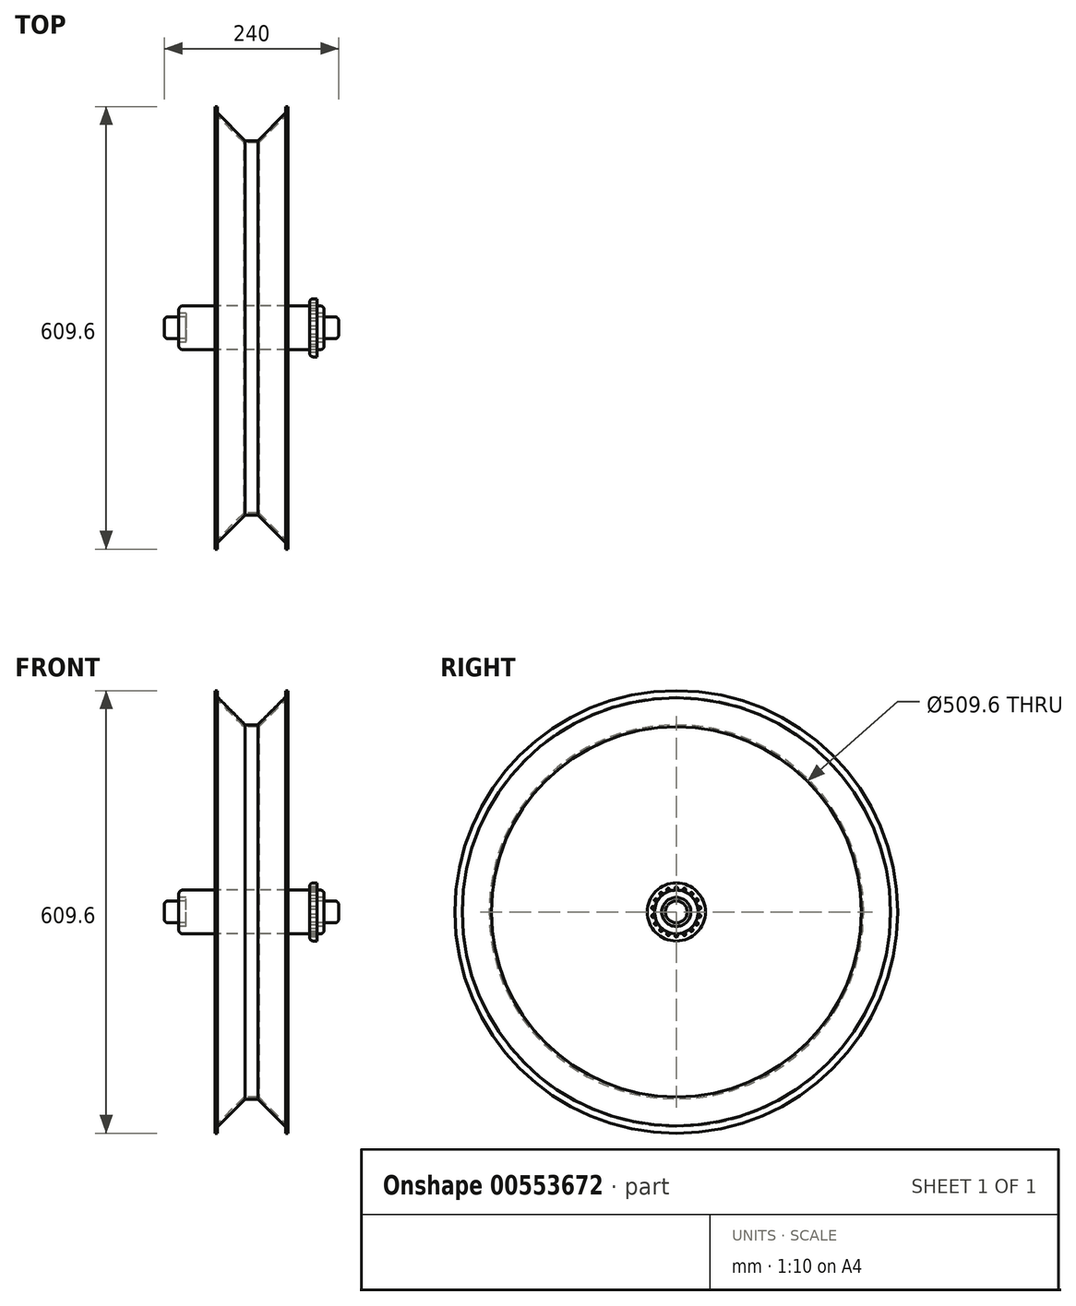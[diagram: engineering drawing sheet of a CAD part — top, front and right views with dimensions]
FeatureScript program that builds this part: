
annotation { "Feature Type Name" : "Feature", "Feature Type Description" : "" }
export const myFeature = defineFeature(function(context is Context, id is Id, definition is map)
    precondition{}
    {
        {
            var Q0;
            Q0=qCreatedBy(makeId("Front.planeOp"),FACE);
            var sketch = newSketch(context, id + "F0", { "sketchPlane" : qUnion([Q0])});
            skLineSegment(sketch, "E0", {"start": v(0, 0) * mm, "end": v(0, 304.8) * mm, "construction": true});
            skLineSegment(sketch, "E1", {"start": v(0, 0) * mm, "end": v(0, 254.8) * mm, "construction": true});
            skLineSegment(sketch, "E2", {"start": v(0, 304.8) * mm, "end": v(-50, 304.8) * mm, "construction": true});
            skLineSegment(sketch, "E3", {"start": v(0, 304.8) * mm, "end": v(50, 304.8) * mm, "construction": true});
            skPoint(sketch, "E4", {"position": v(-50, 304.8) * mm});
            skPoint(sketch, "E5", {"position": v(50, 304.8) * mm});
            skLineSegment(sketch, "E6", {"start": v(-50, 294.8) * mm, "end": v(-10, 254.8) * mm});
            skLineSegment(sketch, "E7", {"start": v(-50, 294.8) * mm, "end": v(-50, 304.8) * mm});
            skLineSegment(sketch, "E8", {"start": v(-10, 254.8) * mm, "end": v(0, 254.8) * mm});
            skLineSegment(sketch, "E9", {"start": v(50, 304.8) * mm, "end": v(50, 294.8) * mm});
            skLineSegment(sketch, "E10", {"start": v(50, 294.8) * mm, "end": v(10, 254.8) * mm});
            skLineSegment(sketch, "E11", {"start": v(10, 254.8) * mm, "end": v(0, 254.8) * mm});
            skLineSegment(sketch, "E12.0", {"start": v(-47, 296.04) * mm, "end": v(-47, 304.8) * mm});
            skLineSegment(sketch, "E12.1", {"start": v(-47, 296.04) * mm, "end": v(-8.76, 257.8) * mm});
            skLineSegment(sketch, "E12.2", {"start": v(47, 304.8) * mm, "end": v(47, 296.04) * mm});
            skLineSegment(sketch, "E12.3", {"start": v(47, 296.04) * mm, "end": v(8.76, 257.8) * mm});
            skLineSegment(sketch, "E12.4", {"start": v(8.76, 257.8) * mm, "end": v(0, 257.8) * mm});
            skLineSegment(sketch, "E12.5", {"start": v(-8.76, 257.8) * mm, "end": v(0, 257.8) * mm});
            skLineSegment(sketch, "E13", {"start": v(-47, 304.8) * mm, "end": v(-50, 304.8) * mm});
            skLineSegment(sketch, "E14", {"start": v(47, 304.8) * mm, "end": v(50, 304.8) * mm});
            skLineSegment(sketch, "E15", {"start": v(0, 0) * mm, "end": v(125, 0) * mm, "construction": true});
            skSolve(sketch);
        }
        {
            var Q0;
            Q0 = qSketchRegion(id + "F0", true);
            var Q1;
            Q1=sQuery(id+"F0.wireOp",EDGE,"E15");
            revolve(context, id + "F1", {"entities" : qUnion([Q0]), "axis" : qUnion([Q1]), "revolveType" : RevolveType.FULL});
        }
        {
            var Q0;
            Q0=qCreatedBy(makeId("Right.planeOp"),FACE);
            var sketch = newSketch(context, id + "F2", { "sketchPlane" : qUnion([Q0])});
            skCircle(sketch, "E16", {"center": v(0, 0) * mm, "radius": 15 * mm});
            skSolve(sketch);
        }
        {
            var Q0;
            Q0 = qSketchRegion(id + "F2", true);
            extrude(context, id + "F3", {"entities" : qUnion([Q0]), "endBound" : BoundingType.SYMMETRIC, "depth" : 240 * mm, "offsetDistance" : 25 * mm});
        }
        {
            var Q0;
            Q0=qCreatedBy(makeId("Right.planeOp"),FACE);
            var sketch = newSketch(context, id + "F4", { "sketchPlane" : qUnion([Q0])});
            skCircle(sketch, "E17", {"center": v(0, 0) * mm, "radius": 15 * mm});
            skCircle(sketch, "E18", {"center": v(0, 0) * mm, "radius": 20 * mm});
            skCircle(sketch, "E19", {"center": v(0, 0) * mm, "radius": 30 * mm});
            skCircle(sketch, "E20", {"center": v(0, 0) * mm, "radius": 40 * mm});
            skPoint(sketch, "E21", {"position": v(0, 32.5) * mm});
            skLineSegment(sketch, "E22", {"start": v(0, 0) * mm, "end": v(11.12, 30.54) * mm, "construction": true});
            skPoint(sketch, "E23", {"position": v(11.12, 30.54) * mm});
            skLineSegment(sketch, "E24", {"start": v(0, 0) * mm, "end": v(20.9, 24.9) * mm, "construction": true});
            skLineSegment(sketch, "E25", {"start": v(0, 0) * mm, "end": v(28.15, 16.25) * mm, "construction": true});
            skLineSegment(sketch, "E26", {"start": v(0, 0) * mm, "end": v(32, 5.64) * mm, "construction": true});
            skLineSegment(sketch, "E27", {"start": v(0, 0) * mm, "end": v(32, -5.64) * mm, "construction": true});
            skLineSegment(sketch, "E28", {"start": v(0, 0) * mm, "end": v(28.15, -16.25) * mm, "construction": true});
            skLineSegment(sketch, "E29", {"start": v(0, 0) * mm, "end": v(20.9, -24.9) * mm, "construction": true});
            skLineSegment(sketch, "E30", {"start": v(0, 0) * mm, "end": v(0, -32.5) * mm, "construction": true});
            skLineSegment(sketch, "E31", {"start": v(0, 0) * mm, "end": v(-11.12, -30.54) * mm, "construction": true});
            skLineSegment(sketch, "E32", {"start": v(0, 0) * mm, "end": v(-20.9, -24.9) * mm, "construction": true});
            skLineSegment(sketch, "E33", {"start": v(0, 0) * mm, "end": v(-32, -5.64) * mm, "construction": true});
            skLineSegment(sketch, "E34", {"start": v(0, 0) * mm, "end": v(-32, 5.64) * mm, "construction": true});
            skLineSegment(sketch, "E35", {"start": v(0, 0) * mm, "end": v(-20.9, 24.9) * mm, "construction": true});
            skLineSegment(sketch, "E36", {"start": v(0, 0) * mm, "end": v(-28.15, -16.25) * mm, "construction": true});
            skLineSegment(sketch, "E37", {"start": v(0, 0) * mm, "end": v(11.12, -30.54) * mm, "construction": true});
            skLineSegment(sketch, "E38", {"start": v(0, 0) * mm, "end": v(-28.15, 16.25) * mm, "construction": true});
            skLineSegment(sketch, "E39", {"start": v(0, 0) * mm, "end": v(-11.12, 30.54) * mm, "construction": true});
            skPoint(sketch, "E40", {"position": v(20.9, 24.9) * mm});
            skPoint(sketch, "E41", {"position": v(28.15, 16.25) * mm});
            skPoint(sketch, "E42", {"position": v(32, 5.64) * mm});
            skPoint(sketch, "E43", {"position": v(32, -5.64) * mm});
            skPoint(sketch, "E44", {"position": v(28.15, -16.25) * mm});
            skPoint(sketch, "E45", {"position": v(20.9, -24.9) * mm});
            skPoint(sketch, "E46", {"position": v(11.12, -30.54) * mm});
            skPoint(sketch, "E47", {"position": v(0, -32.5) * mm});
            skPoint(sketch, "E48", {"position": v(-11.12, -30.54) * mm});
            skPoint(sketch, "E49", {"position": v(-20.9, -24.9) * mm});
            skPoint(sketch, "E50", {"position": v(-28.15, -16.25) * mm});
            skPoint(sketch, "E51", {"position": v(-32, -5.64) * mm});
            skPoint(sketch, "E52", {"position": v(-32, 5.64) * mm});
            skPoint(sketch, "E53", {"position": v(-28.15, 16.25) * mm});
            skPoint(sketch, "E54", {"position": v(-20.9, 24.9) * mm});
            skPoint(sketch, "E55", {"position": v(-11.12, 30.54) * mm});
            skSolve(sketch);
        }
        {
            var Q0;
            Q0=makeQuery(id+"F4.imprint","IMPRINT",FACE,{"disambiguationData":[TD([[makeQuery(id+"F4.imprint","IMPRINT",EDGE,{"derivedFrom":sQuery(id+"F4.wireOp",EDGE,"E17")}),-1.0]])]});
            extrude(context, id + "F5", {"entities" : qUnion([Q0]), "operationType" : NewBodyOperationType.ADD, "endBound" : BoundingType.SYMMETRIC, "depth" : 180 * mm, "offsetDistance" : 25 * mm});
        }
        {
            var Q0;
            Q0=makeQuery(id+"F4.imprint","IMPRINT",FACE,{"disambiguationData":[TD([[makeQuery(id+"F4.imprint","IMPRINT",EDGE,{"derivedFrom":sQuery(id+"F4.wireOp",EDGE,"E18")}),-1.0]])]});
            extrude(context, id + "F6", {"entities" : qUnion([Q0]), "operationType" : NewBodyOperationType.ADD, "endBound" : BoundingType.SYMMETRIC, "depth" : 200 * mm, "offsetDistance" : 25 * mm});
        }
        {
            var Q0;
            Q0=makeQuery(id+"F4.imprint","IMPRINT",FACE,{"disambiguationData":[TD([[makeQuery(id+"F4.imprint","IMPRINT",EDGE,{"derivedFrom":sQuery(id+"F4.wireOp",EDGE,"E19")}),-1.0]])]});
            var Q1;
            Q1=makeQuery(id+"F5.opExtrude","CAP_FACE",FACE,{"disambiguationData":[OSD([sQuery(id+"F4.wireOp",EDGE,"E17"),sQuery(id+"F4.wireOp",EDGE,"E18")])],"isStart":false});
            extrude(context, id + "F7", {"entities" : qUnion([Q0]), "endBound" : BoundingType.UP_TO_SURFACE, "depth" : 182 * mm, "endBoundEntityFace" : qUnion([Q1]), "offsetDistance" : 25 * mm, "hasSecondDirection" : true, "secondDirectionOppositeDirection" : false, "secondDirectionDepth" : 80 * mm});
        }
        {
            var Q0;
            Q0=makeQuery(id+"F3.opExtrude","CAP_EDGE",EDGE,{"disambiguationData":[OSD([sQuery(id+"F2.wireOp",EDGE,"E16")])],"isStart":false});
            var Q1;
            Q1=makeQuery(id+"F3.opExtrude","CAP_EDGE",EDGE,{"disambiguationData":[OSD([sQuery(id+"F2.wireOp",EDGE,"E16")])],"isStart":true});
            var Q2;
            Q2=makeQuery(id+"F6.opExtrude","CAP_EDGE",EDGE,{"disambiguationData":[OSD([sQuery(id+"F4.wireOp",EDGE,"E19")])],"isStart":true});
            var Q3;
            Q3=makeQuery(id+"F6.opExtrude","CAP_EDGE",EDGE,{"disambiguationData":[OSD([sQuery(id+"F4.wireOp",EDGE,"E19")])],"isStart":false});
            var Q4;
            Q4=makeQuery(id+"FDHI70p1gNgxUke_2.opExtrude","TWEAK_EDGE",EDGE,{"derivedFrom":[makeQuery(id+"F4.imprint","IMPRINT",EDGE,{"derivedFrom":sQuery(id+"F4.wireOp",EDGE,"E20")}),makeQuery(id+"F5.opExtrude","CAP_FACE",FACE,{"disambiguationData":[OSD([sQuery(id+"F4.wireOp",EDGE,"E17"),sQuery(id+"F4.wireOp",EDGE,"E18")])],"isStart":true})]});
            var Q5;
            Q5=makeQuery(id+"FDHI70p1gNgxUke_2.opExtrude","CAP_EDGE",EDGE,{"disambiguationData":[OSD([sQuery(id+"F4.wireOp",EDGE,"E20")])],"isStart":true});
            var Q6;
            Q6=makeQuery(id+"F7.opExtrude","CAP_EDGE",EDGE,{"disambiguationData":[OSD([sQuery(id+"F4.wireOp",EDGE,"E20")])],"isStart":true});
            var Q7;
            Q7=makeQuery(id+"F7.opExtrude","TWEAK_EDGE",EDGE,{"derivedFrom":[makeQuery(id+"F4.imprint","IMPRINT",EDGE,{"derivedFrom":sQuery(id+"F4.wireOp",EDGE,"E20")}),makeQuery(id+"F5.opExtrude","CAP_FACE",FACE,{"disambiguationData":[OSD([sQuery(id+"F4.wireOp",EDGE,"E17"),sQuery(id+"F4.wireOp",EDGE,"E18")])],"isStart":false})]});
            fillet(context, id + "F8", {"entities" : qUnion([Q0, Q1, Q2, Q3, Q4, Q5, Q6, Q7]), "radius" : 5 * mm, "tangentPropagation" : true, "allowEdgeOverflow" : false});
        }
        {
            var Q0;
            Q0=sQuery(id+"F4.wireOp",VERTEX,"E21");
            var Q1;
            Q1=sQuery(id+"F4.wireOp",VERTEX,"E23");
            var Q2;
            Q2=sQuery(id+"F4.wireOp",VERTEX,"E40");
            var Q3;
            Q3=sQuery(id+"F4.wireOp",VERTEX,"E41");
            var Q4;
            Q4=sQuery(id+"F4.wireOp",VERTEX,"E42");
            var Q5;
            Q5=sQuery(id+"F4.wireOp",VERTEX,"E43");
            var Q6;
            Q6=sQuery(id+"F4.wireOp",VERTEX,"E44");
            var Q7;
            Q7=sQuery(id+"F4.wireOp",VERTEX,"E45");
            var Q8;
            Q8=sQuery(id+"F4.wireOp",VERTEX,"E46");
            var Q9;
            Q9=sQuery(id+"F4.wireOp",VERTEX,"E47");
            var Q10;
            Q10=sQuery(id+"F4.wireOp",VERTEX,"E48");
            var Q11;
            Q11=sQuery(id+"F4.wireOp",VERTEX,"E49");
            var Q12;
            Q12=sQuery(id+"F4.wireOp",VERTEX,"E49");
            var Q13;
            Q13=sQuery(id+"F4.wireOp",VERTEX,"E50");
            var Q14;
            Q14=sQuery(id+"F4.wireOp",VERTEX,"E51");
            var Q15;
            Q15=sQuery(id+"F4.wireOp",VERTEX,"E52");
            var Q16;
            Q16=sQuery(id+"F4.wireOp",VERTEX,"E53");
            var Q17;
            Q17=sQuery(id+"F4.wireOp",VERTEX,"E54");
            var Q18;
            Q18=sQuery(id+"F4.wireOp",VERTEX,"E55");
            var Q19;
            Q19=makeQuery(id+"F7.opExtrude","SWEPT_BODY",BODY,{"disambiguationData":[OSD([sQuery(id+"F4.wireOp",EDGE,"E19"),sQuery(id+"F4.wireOp",EDGE,"E20")])]});
            var Q20;
            Q20=makeQuery(id+"F3.opExtrude","SWEPT_BODY",BODY,{"disambiguationData":[OSD([sQuery(id+"F2.wireOp",EDGE,"E16")])]});
            hole(context, id + "F9", {"style" : HoleStyle.SIMPLE, "endStyle" : HoleEndStyle.BLIND, "oppositeDirection" : true, "standardTappedOrClearance" : lookupTablePath({ "standard" : "ISO", "size" : "4", "type" : "Drilled" }), "standardBlindInLast" : lookupTablePath({ "standard" : "ISO", "size" : "4", "type" : "Drilled" }), "holeDiameter" : 4 * mm, "holeDepth" : 16 * mm, "isTappedThrough" : true, "tappedDepth" : 12 * mm, "tapClearance" : 3, "locations" : qUnion([Q0, Q1, Q2, Q3, Q4, Q5, Q6, Q7, Q8, Q9, Q10, Q11, Q12, Q13, Q14, Q15, Q16, Q17, Q18]), "scope" : qUnion([Q19, Q20])});
        }
    });
